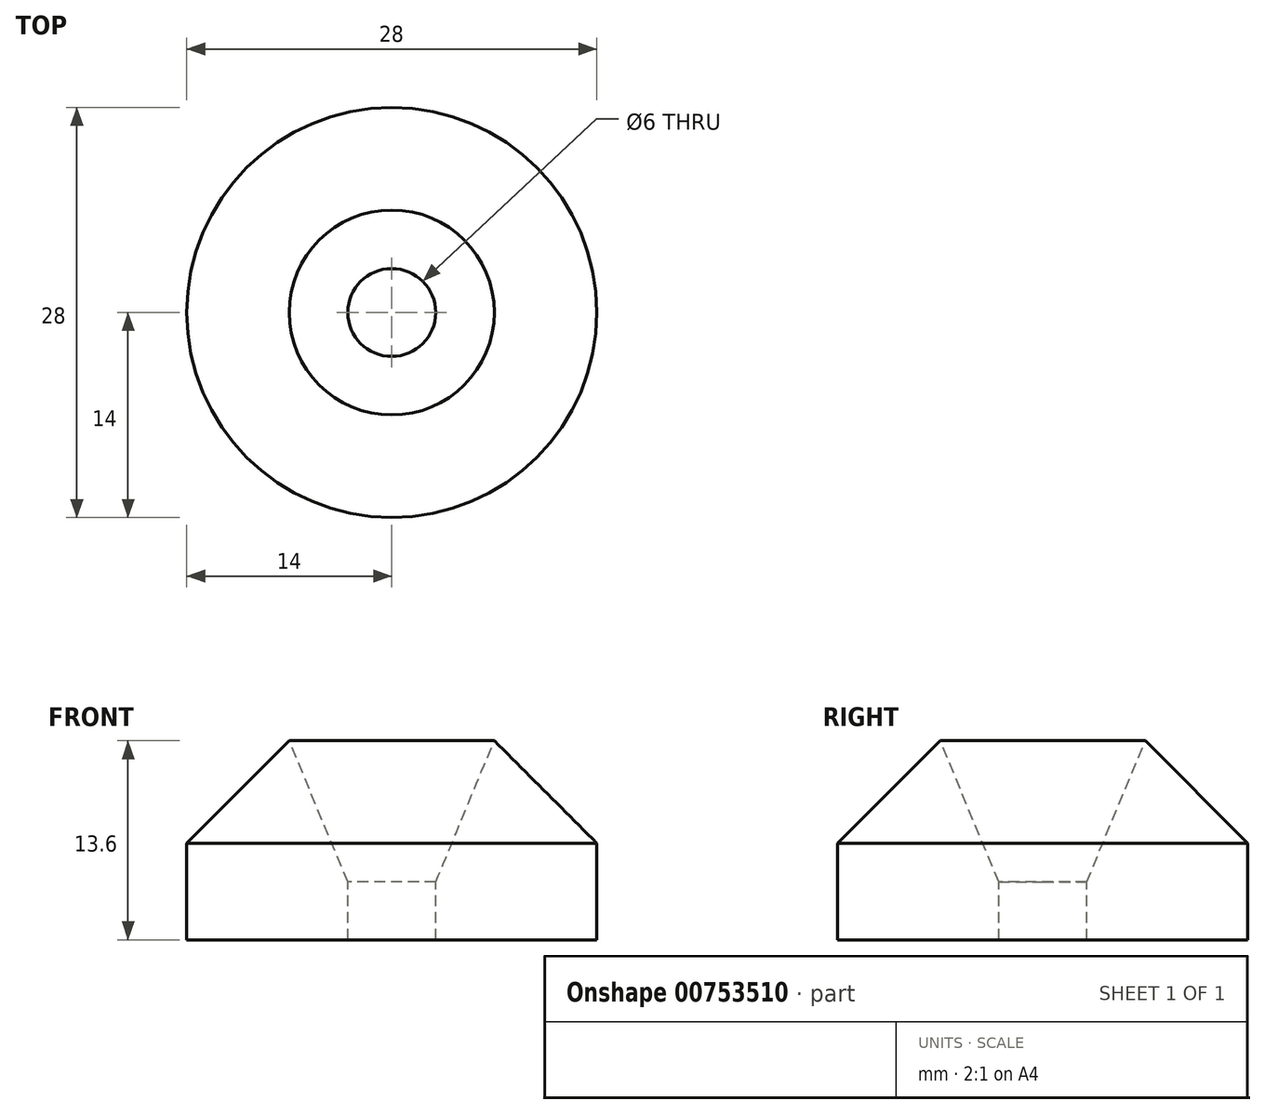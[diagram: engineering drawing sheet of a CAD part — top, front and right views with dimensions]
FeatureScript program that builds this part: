
annotation { "Feature Type Name" : "Feature", "Feature Type Description" : "" }
export const myFeature = defineFeature(function(context is Context, id is Id, definition is map)
    precondition{}
    {
        {
            var Q0;
            Q0=qCreatedBy(makeId("Top.planeOp"),FACE);
            var sketch = newSketch(context, id + "F0", { "sketchPlane" : qUnion([Q0])});
            skCircle(sketch, "E0", {"center": v(0, 0) * mm, "radius": 14 * mm});
            skSolve(sketch);
        }
        {
            var Q0;
            Q0 = qSketchRegion(id + "F0", true);
            extrude(context, id + "F1", {"entities" : qUnion([Q0]), "depth" : 14.6 * mm, "offsetDistance" : 25.4 * mm});
        }
        {
            var Q0;
            Q0=makeQuery(id+"F1.opExtrude","CAP_FACE",FACE,{"disambiguationData":[OSD([sQuery(id+"F0.wireOp",EDGE,"E0")])],"isStart":false});
            var sketch = newSketch(context, id + "F2", { "sketchPlane" : qUnion([Q0])});
            skPoint(sketch, "E1", {"position": v(0, 0) * mm});
            skSolve(sketch);
        }
        {
            var Q0;
            Q0=makeQuery(id+"F1.opExtrude","CAP_FACE",FACE,{"disambiguationData":[OSD([sQuery(id+"F0.wireOp",EDGE,"E0")])],"isStart":false});
            chamfer(context, id + "F3", {"entities" : qUnion([Q0]), "width" : 8 * mm, "tangentPropagation" : true});
        }
        {
            var Q0;
            Q0=sQuery(id+"F2.wireOp",VERTEX,"E1");
            var Q1;
            Q1=makeQuery(id+"F1.opExtrude","SWEPT_BODY",BODY,{"disambiguationData":[OSD([sQuery(id+"F0.wireOp",EDGE,"E0")])]});
            hole(context, id + "F4", {"style" : HoleStyle.C_SINK, "endStyle" : HoleEndStyle.THROUGH, "holeDiameter" : 6 * mm, "cSinkDiameter" : 14 * mm, "cSinkAngle" : 45 * degree, "majorDiameter" : 5 * mm, "isTappedThrough" : true, "tappedDepth" : 12 * mm, "tapClearance" : 3, "locations" : qUnion([Q0]), "scope" : qUnion([Q1])});
        }
    });
